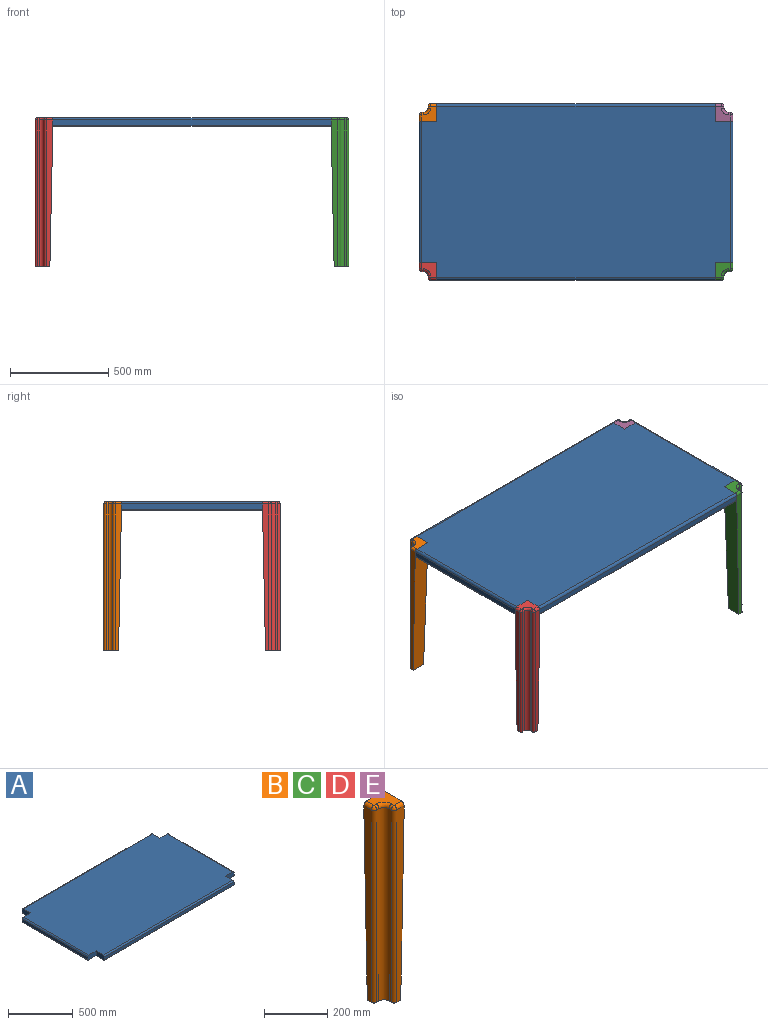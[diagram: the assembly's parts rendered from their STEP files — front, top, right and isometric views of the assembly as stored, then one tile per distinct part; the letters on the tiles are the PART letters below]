
ASSEMBLY  parts=5 mates=4
PART A: 22 faces, bbox 1600x900x45 mm
  f0: plane 1590x890mm, normal (0,0,-1), area 1386200mm2, adj f6,f7,f8,f9,f10,f11,f12,f13
  f1: plane 1575x875mm, normal (0,0,1), area 1354100mm2, adj f6,f7,f8,f9,f10,f11,f12,f13
  f2: plane 1420x27.5mm, normal (0,1,0), area 39050mm2, adj f11,f13,f14,f18
  f3: plane 1420x27.5mm, normal (0,-1,0), area 39050mm2, adj f7,f9,f16,f20
  f4: plane 720x27.5mm, normal (1,0,0), area 19800mm2, adj f8,f12,f15,f19
  f5: plane 720x27.5mm, normal (-1,0,0), area 19800mm2, adj f6,f10,f17,f21
  f6: plane 90x45mm, normal (0,-1,0), area 4011.1mm2, adj f0,f1,f5,f7,f17,f21
  f7: plane 90x45mm, normal (-1,0,0), area 4011.1mm2, adj f0,f1,f3,f6,f16,f20
  f8: plane 90x45mm, normal (0,-1,0), area 4011.1mm2, adj f0,f1,f4,f9,f15,f19
  f9: plane 90x45mm, normal (1,0,0), area 4011.1mm2, adj f0,f1,f3,f8,f16,f20
  f10: plane 90x45mm, normal (0,1,0), area 4011.1mm2, adj f0,f1,f5,f11,f17,f21
  f11: plane 90x45mm, normal (-1,0,0), area 4011.1mm2, adj f0,f1,f2,f10,f14,f18
  f12: plane 90x45mm, normal (0,1,0), area 4011.1mm2, adj f0,f1,f4,f13,f15,f19
  f13: plane 90x45mm, normal (1,0,0), area 4011.1mm2, adj f0,f1,f2,f12,f14,f18
  f14: cylinder r=12.5mm len=1420mm, axis (1,0,0), area 27881.6mm2, adj f1,f2,f11,f13
  f15: cylinder r=12.5mm len=720mm, axis (0,-1,0), area 14137.2mm2, adj f1,f4,f8,f12
  f16: cylinder r=12.5mm len=1420mm, axis (-1,0,0), area 27881.6mm2, adj f1,f3,f7,f9
  f17: cylinder r=12.5mm len=720mm, axis (0,1,0), area 14137.2mm2, adj f1,f5,f6,f10
  f18: cylinder r=5mm len=1420mm, axis (-1,0,0), area 11152.7mm2, adj f0,f2,f11,f13
  f19: cylinder r=5mm len=720mm, axis (0,1,0), area 5654.9mm2, adj f0,f4,f8,f12
  f20: cylinder r=5mm len=1420mm, axis (1,0,0), area 11152.7mm2, adj f0,f3,f7,f9
  f21: cylinder r=5mm len=720mm, axis (0,-1,0), area 5654.9mm2, adj f0,f5,f6,f10
PART B: 20 faces, bbox 90x90x760 mm
  f0: plane 75x75mm, normal (0,0,-1), area 3641.6mm2, adj f1,f3,f6,f7,f8,f9,f15,f18
  f1: plane 747.5x32.5mm, normal (0,-1,0), area 18968.8mm2, adj f0,f2,f16,f18,f19
  f2: plane 90x50mm, normal (1,0,0), area 4466.5mm2, adj f1,f4,f5,f16,f19
  f3: plane 710x90mm, normal (0,1,-0.02), area 58588.1mm2, adj f0,f5,f6,f19
  f4: plane 77.5x77.5mm, normal (0,0,1), area 4244.1mm2, adj f2,f5,f10,f11,f12,f13,f16
  f5: plane 90x50mm, normal (0,1,0), area 4466.5mm2, adj f2,f3,f4,f6,f13
  f6: plane 747.5x32.5mm, normal (-1,0,0), area 18968.8mm2, adj f0,f3,f5,f13,f15
  f7: plane 747.5x10mm, normal (0,-1,0), area 7475mm2, adj f0,f9,f12,f15
  f8: plane 747.5x10mm, normal (-1,0,0), area 7475mm2, adj f0,f9,f10,f18
  f9: cylinder r=22.5mm len=747.5mm, axis (0,0,1), area 26418.8mm2, adj f0,f7,f8,f11
  f10: cylinder r=12.5mm len=12.5mm, axis (0,-1,0), area 196.3mm2, adj f4,f8,f11,f17
  f11: torus R=35mm, axis (0,0,1), area 834.1mm2, adj f4,f9,f10,f12
  f12: cylinder r=12.5mm len=12.5mm, axis (1,0,0), area 196.3mm2, adj f4,f7,f11,f14
  f13: cylinder r=12.5mm len=32.5mm, axis (0,-1,0), area 638.1mm2, adj f4,f5,f6,f14
  f14: sphere r=12.5mm, area 245.4mm2, adj f12,f13,f15
  f15: cylinder r=12.5mm len=747.5mm, axis (0,0,-1), area 14677.1mm2, adj f0,f6,f7,f14
  f16: cylinder r=12.5mm len=32.5mm, axis (1,0,0), area 638.1mm2, adj f1,f2,f4,f17
  f17: sphere r=12.5mm, area 245.4mm2, adj f10,f16,f18
  f18: cylinder r=12.5mm len=747.5mm, axis (0,0,1), area 14677.1mm2, adj f0,f1,f8,f17
  f19: plane 710x90mm, normal (1,0,-0.02), area 58588.1mm2, adj f0,f1,f2,f3
PART C: same geometry as B
PART D: same geometry as B
PART E: same geometry as B
PLACE A t=(-1.83,59.01,67.6)mm
PLACE B rot(axis=(0,0,-1),90deg) t=(-756.83,464.01,112.6)mm
PLACE C rot(axis=(0,0,1),90deg) t=(753.17,-345.99,112.6)mm
PLACE D t=(-756.83,-345.99,112.6)mm
PLACE E rot(axis=(0,0,1),180deg) t=(753.17,464.01,112.6)mm
MATE fastened E.f4 <-> A.f1  axis (0,0,1) through (708.17,419.01,112.6)mm
MATE fastened D.f4 <-> A.f1  axis (0,0,1) through (-711.83,-300.99,112.6)mm
MATE fastened C.f4 <-> A.f1  axis (0,0,1) through (708.17,-300.99,112.6)mm
MATE fastened B.f4 <-> A.f1  axis (0,0,1) through (-711.83,419.01,112.6)mm
